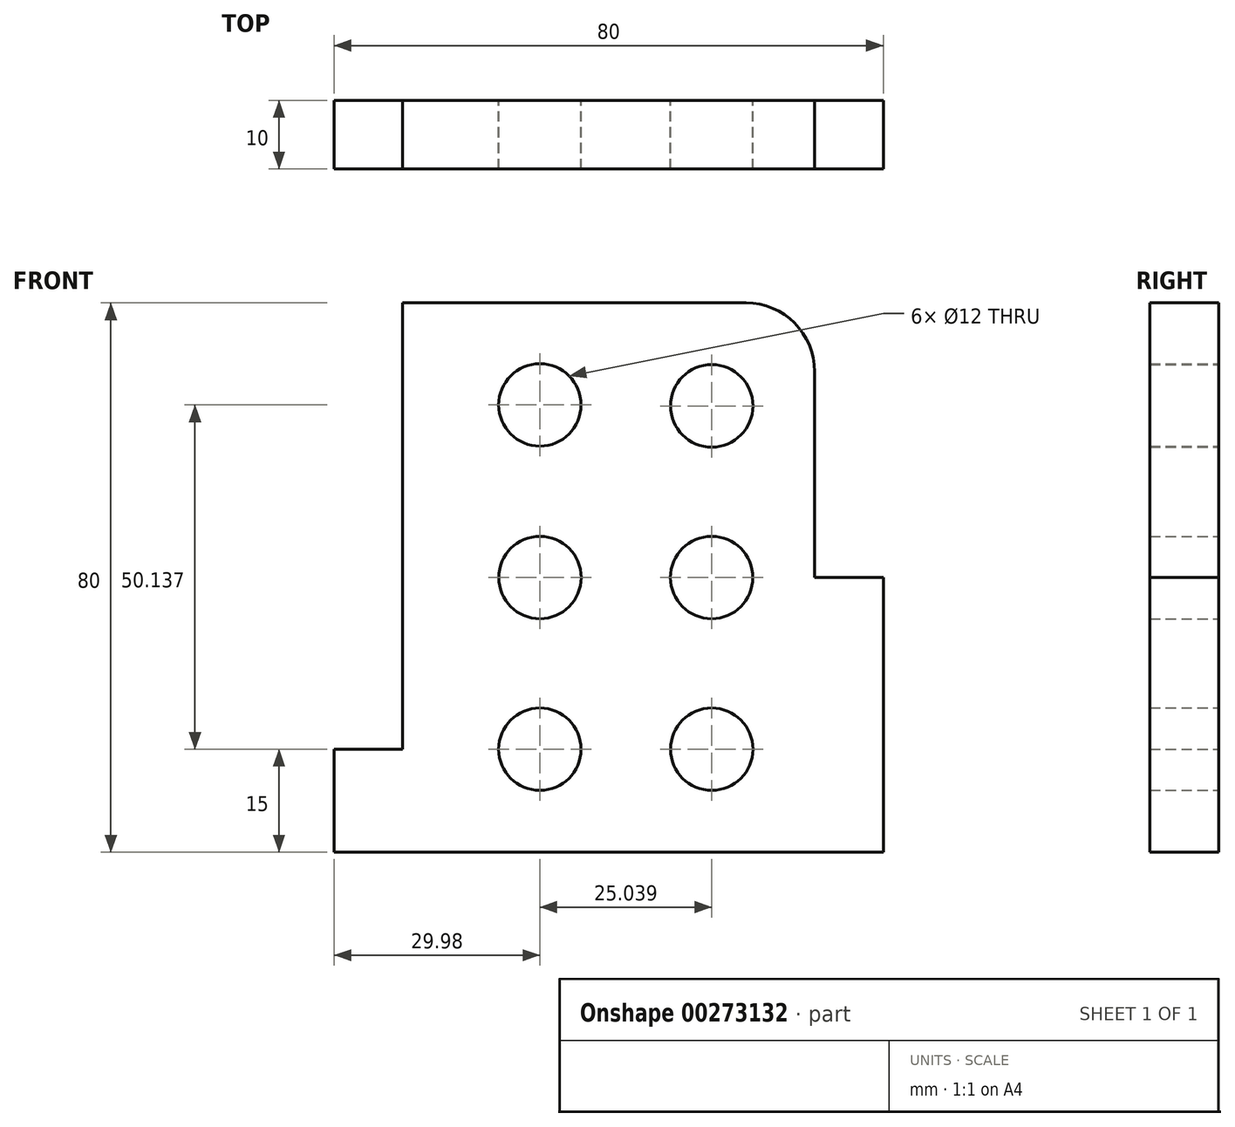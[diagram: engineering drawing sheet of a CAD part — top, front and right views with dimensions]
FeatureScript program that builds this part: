
annotation { "Feature Type Name" : "Feature", "Feature Type Description" : "" }
export const myFeature = defineFeature(function(context is Context, id is Id, definition is map)
    precondition{}
    {
        {
            var Q0;
            Q0=qCreatedBy(makeId("Front.planeOp"),FACE);
            var sketch = newSketch(context, id + "F0", { "sketchPlane" : qUnion([Q0])});
            skLineSegment(sketch, "E0", {"start": v(0, 0) * mm, "end": v(0, 15) * mm});
            skLineSegment(sketch, "E1", {"start": v(0, 0) * mm, "end": v(80, 0) * mm});
            skLineSegment(sketch, "E2", {"start": v(0, 15) * mm, "end": v(10, 15) * mm});
            skLineSegment(sketch, "E3", {"start": v(10, 15) * mm, "end": v(10, 80) * mm});
            skLineSegment(sketch, "E4", {"start": v(80, 0) * mm, "end": v(80, 40) * mm});
            skLineSegment(sketch, "E5", {"start": v(80, 40) * mm, "end": v(70, 40) * mm});
            skCircle(sketch, "E6", {"center": v(30, 40) * mm, "radius": 6 * mm});
            skCircle(sketch, "E7", {"center": v(55, 40) * mm, "radius": 6 * mm});
            skCircle(sketch, "E8", {"center": v(55.02, 15) * mm, "radius": 6 * mm});
            skCircle(sketch, "E9", {"center": v(29.98, 15) * mm, "radius": 6 * mm});
            skCircle(sketch, "E10", {"center": v(29.98, 65.14) * mm, "radius": 6 * mm});
            skCircle(sketch, "E11", {"center": v(55.02, 65) * mm, "radius": 6 * mm});
            skLineSegment(sketch, "E12", {"start": v(29.98, 65.14) * mm, "end": v(55.02, 65) * mm, "construction": true});
            skLineSegment(sketch, "E13", {"start": v(30, 40) * mm, "end": v(55, 40) * mm, "construction": true});
            skLineSegment(sketch, "E14", {"start": v(29.98, 15) * mm, "end": v(55.02, 15) * mm, "construction": true});
            skLineSegment(sketch, "E15", {"start": v(29.98, 65.14) * mm, "end": v(29.98, 15) * mm, "construction": true});
            skLineSegment(sketch, "E16", {"start": v(55.02, 65) * mm, "end": v(55.02, 15) * mm, "construction": true});
            skArc(sketch, "E17", {"start": v(70, 70) * mm, "mid": v(67.07, 77.07) * mm, "end": v(60, 80) * mm});
            skLineSegment(sketch, "E18", {"start": v(70, 70) * mm, "end": v(70, 40) * mm});
            skLineSegment(sketch, "E19", {"start": v(10, 80) * mm, "end": v(60, 80) * mm});
            skSolve(sketch);
        }
        {
            var Q0;
            Q0=makeQuery(id+"F0.imprint","IMPRINT",FACE,{"disambiguationData":[TD([[makeQuery(id+"F0.imprint","IMPRINT",EDGE,{"derivedFrom":sQuery(id+"F0.wireOp",EDGE,"E0")}),-1.0]])]});
            extrude(context, id + "F1", {"entities" : qUnion([Q0]), "depth" : 10 * mm});
        }
    });
